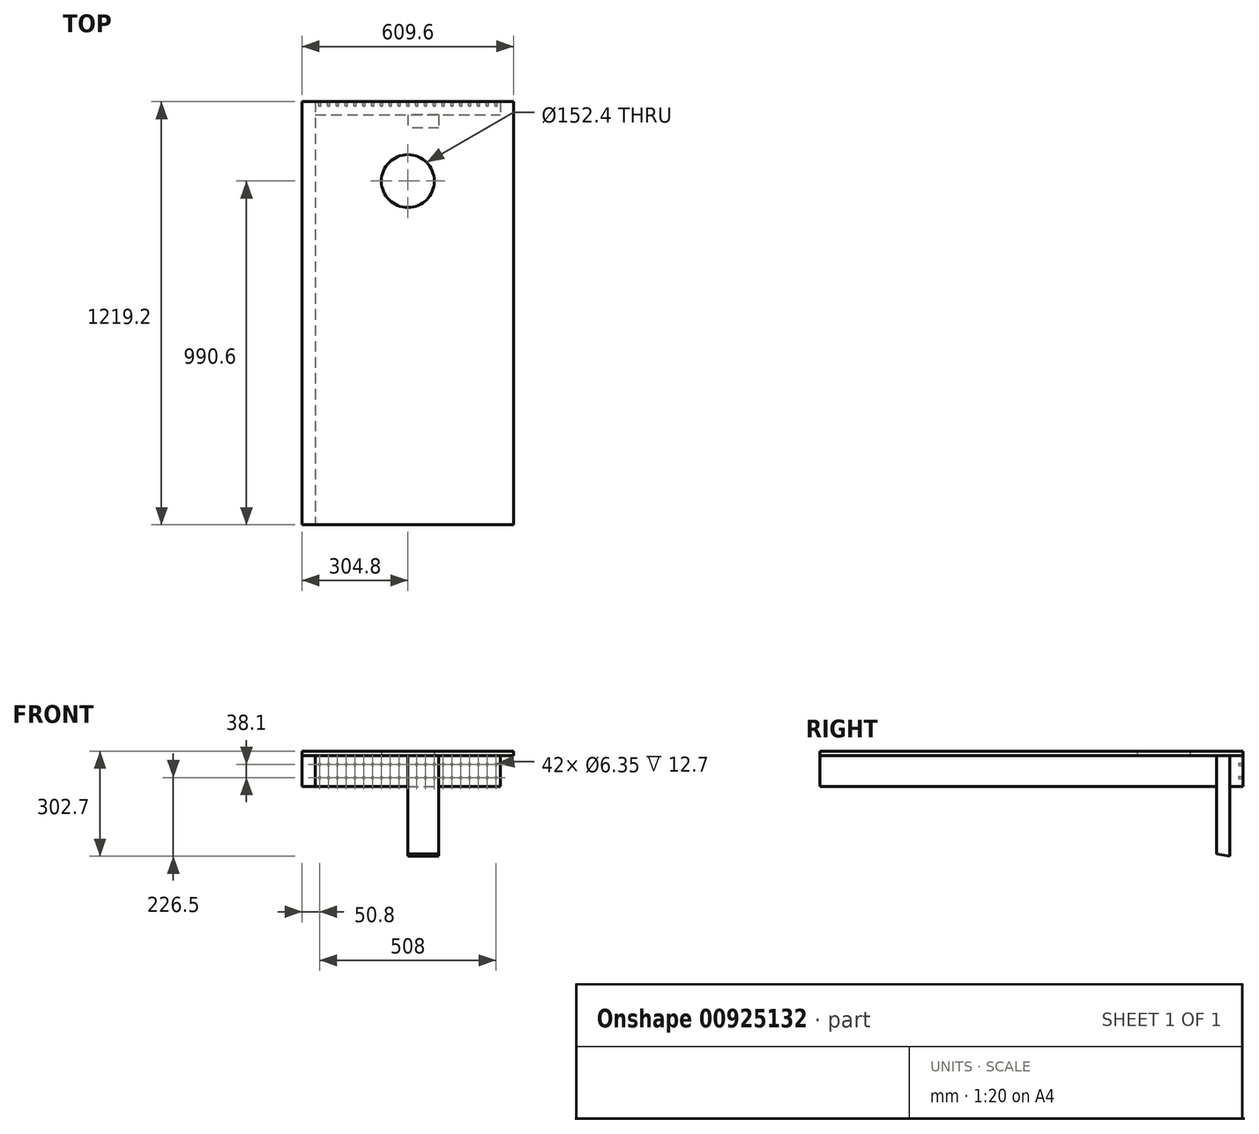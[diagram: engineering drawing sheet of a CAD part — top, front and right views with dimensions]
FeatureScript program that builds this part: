
annotation { "Feature Type Name" : "Feature", "Feature Type Description" : "" }
export const myFeature = defineFeature(function(context is Context, id is Id, definition is map)
    precondition{}
    {
        {
            assignVariable(context, id + "F0", {"name" : "sheetThickness", "anyValue" : 12.7 * mm});
        }
        {
            assignVariable(context, id + "F1", {"name" : "stockWidth", "anyValue" : 88.9 * mm});
        }
        {
            var Q0;
            Q0=qCreatedBy(makeId("Top.planeOp"),FACE);
            var sketch = newSketch(context, id + "F2", { "sketchPlane" : qUnion([Q0])});
            skLineSegment(sketch, "E0.bottom", {"start": v(304.8, -609.6) * mm, "end": v(-304.8, -609.6) * mm});
            skLineSegment(sketch, "E0.top", {"start": v(304.8, 609.6) * mm, "end": v(-304.8, 609.6) * mm});
            skLineSegment(sketch, "E0.left", {"start": v(304.8, -609.6) * mm, "end": v(304.8, 609.6) * mm});
            skLineSegment(sketch, "E0.right", {"start": v(-304.8, -609.6) * mm, "end": v(-304.8, 609.6) * mm});
            skPoint(sketch, "E0.middle", {"position": v(0, 0) * mm});
            skLineSegment(sketch, "E1", {"start": v(0, 609.6) * mm, "end": v(0, 381) * mm, "construction": true});
            skCircle(sketch, "E2", {"center": v(0, 381) * mm, "radius": 76.2 * mm});
            skLineSegment(sketch, "E3", {"start": v(-266.7, 571.5) * mm, "end": v(266.7, 571.5) * mm});
            skLineSegment(sketch, "E4", {"start": v(-266.7, -571.5) * mm, "end": v(266.7, -571.5) * mm});
            skLineSegment(sketch, "E5", {"start": v(266.7, 609.6) * mm, "end": v(266.7, -609.6) * mm});
            skLineSegment(sketch, "E6", {"start": v(-266.7, 609.6) * mm, "end": v(-266.7, -609.6) * mm});
            skLineSegment(sketch, "E7.bottom", {"start": v(-241.3, 571.5) * mm, "end": v(-152.4, 571.5) * mm});
            skLineSegment(sketch, "E7.top", {"start": v(-241.3, 533.4) * mm, "end": v(-152.4, 533.4) * mm});
            skLineSegment(sketch, "E7.left", {"start": v(-241.3, 571.5) * mm, "end": v(-241.3, 533.4) * mm});
            skLineSegment(sketch, "E7.right", {"start": v(-152.4, 571.5) * mm, "end": v(-152.4, 533.4) * mm});
            skLineSegment(sketch, "E8.bottom", {"start": v(152.4, 571.5) * mm, "end": v(241.3, 571.5) * mm});
            skLineSegment(sketch, "E8.top", {"start": v(152.4, 533.4) * mm, "end": v(241.3, 533.4) * mm});
            skLineSegment(sketch, "E8.left", {"start": v(152.4, 571.5) * mm, "end": v(152.4, 533.4) * mm});
            skLineSegment(sketch, "E8.right", {"start": v(241.3, 571.5) * mm, "end": v(241.3, 533.4) * mm});
            skLineSegment(sketch, "E9.bottom", {"start": v(266.7, -19.05) * mm, "end": v(-266.7, -19.05) * mm});
            skLineSegment(sketch, "E9.top", {"start": v(266.7, 19.05) * mm, "end": v(-266.7, 19.05) * mm});
            skLineSegment(sketch, "E9.left", {"start": v(266.7, -19.05) * mm, "end": v(266.7, 19.05) * mm});
            skLineSegment(sketch, "E9.right", {"start": v(-266.7, -19.05) * mm, "end": v(-266.7, 19.05) * mm});
            skSolve(sketch);
        }
        {
            var Q0;
            Q0=makeQuery(id+"F2.imprint","IMPRINT",FACE,{"disambiguationData":[TD([[makeQuery(id+"F2.imprint","IMPRINT",EDGE,{"derivedFrom":sQuery(id+"F2.wireOp",EDGE,"E2")}),-1.0]])]});
            var Q1;
            Q1=makeQuery(id+"F2.imprint","IMPRINT",FACE,{"disambiguationData":[TD([[makeQuery(id+"F2.imprint","IMPRINT",EDGE,{"derivedFrom":sQuery(id+"F2.wireOp",EDGE,"E7.top")}),1.0]])]});
            var Q2;
            Q2=makeQuery(id+"F2.imprint","IMPRINT",FACE,{"disambiguationData":[TD([[makeQuery(id+"F2.imprint","IMPRINT",EDGE,{"derivedFrom":sQuery(id+"F2.wireOp",EDGE,"E8.top")}),1.0]])]});
            var Q3;
            {var subQ5=sQuery(id+"F2.wireOp",EDGE,"E0.left");Q3=makeQuery(id+"F2.imprint","IMPRINT",FACE,{"disambiguationData":[TD([[makeQuery(id+"F2.imprint","IMPRINT",EDGE,{"derivedFrom":subQ5}),1.0]])]});}
            var Q4;
            {var subQ4=sQuery(id+"F2.wireOp",EDGE,"E0.top");var subQ10=sQuery(id+"F2.wireOp",EDGE,"E5");var subQ11=makeQuery(id+"F2.imprint","INTERSECT",VERTEX,{"derivedFrom":[subQ4,subQ10]});var subQ18=sQuery(id+"F2.wireOp",EDGE,"E0.left");var subQ23=sQuery(id+"F2.wireOp",EDGE,"E0.right");Q4=qUnion([makeQuery(id+"F2.imprint","IMPRINT",FACE,{"disambiguationData":[TD([[makeQuery(id+"F2.imprint","IMPRINT",EDGE,{"derivedFrom":subQ23}),-1.0]])]}),makeQuery(id+"F2.imprint","IMPRINT",FACE,{"disambiguationData":[TD([[makeQuery(id+"F2.imprint","IMPRINT",EDGE,{"derivedFrom":subQ18}),1.0]])]}),makeQuery(id+"F2.imprint","IMPRINT",FACE,{"disambiguationData":[TD([[makeQuery(id+"F2.imprint","IMPRINT",EDGE,{"disambiguationData":[TD([[subQ11,-1.0]])],"derivedFrom":subQ4}),1.0]])]})]);}
            var Q5;
            {var subQ0=sQuery(id+"F2.wireOp",EDGE,"E0.right");Q5=makeQuery(id+"F2.imprint","IMPRINT",FACE,{"disambiguationData":[TD([[makeQuery(id+"F2.imprint","IMPRINT",EDGE,{"derivedFrom":subQ0}),-1.0]])]});}
            var Q6;
            {var subQ5=sQuery(id+"F2.wireOp",EDGE,"E4");Q6=makeQuery(id+"F2.imprint","IMPRINT",FACE,{"disambiguationData":[TD([[makeQuery(id+"F2.imprint","IMPRINT",EDGE,{"derivedFrom":subQ5}),-1.0]])]});}
            var Q7;
            {var subQ0=sQuery(id+"F2.wireOp",EDGE,"E4");Q7=makeQuery(id+"F2.imprint","IMPRINT",FACE,{"disambiguationData":[TD([[makeQuery(id+"F2.imprint","IMPRINT",EDGE,{"derivedFrom":subQ0}),1.0]])]});}
            var Q8;
            {var subQ0=sQuery(id+"F2.wireOp",EDGE,"E9.bottom");Q8=makeQuery(id+"F2.imprint","IMPRINT",FACE,{"disambiguationData":[TD([[makeQuery(id+"F2.imprint","IMPRINT",EDGE,{"derivedFrom":subQ0}),-1.0]])]});}
            extrude(context, id + "F3", {"entities" : qUnion([Q0, Q1, Q2, Q3, Q4, Q5, Q6, Q7, Q8]), "depth" : getVariable(context, 'sheetThickness'), "offsetDistance" : 25.4 * mm});
        }
        {
            var Q0;
            {var subQ4=sQuery(id+"F2.wireOp",EDGE,"E0.top");var subQ9=sQuery(id+"F2.wireOp",EDGE,"E5");var subQ10=makeQuery(id+"F2.imprint","INTERSECT",VERTEX,{"derivedFrom":[subQ4,subQ9]});Q0=makeQuery(id+"F2.imprint","IMPRINT",FACE,{"disambiguationData":[TD([[makeQuery(id+"F2.imprint","IMPRINT",EDGE,{"disambiguationData":[TD([[subQ10,-1.0]])],"derivedFrom":subQ4}),1.0]])]});}
            extrude(context, id + "F4", {"entities" : qUnion([Q0]), "oppositeDirection" : true, "depth" : getVariable(context, 'stockWidth'), "offsetDistance" : 25.4 * mm});
        }
        {
            var Q0;
            {var subQ0=sQuery(id+"F2.wireOp",EDGE,"E0.right");Q0=makeQuery(id+"F2.imprint","IMPRINT",FACE,{"disambiguationData":[TD([[makeQuery(id+"F2.imprint","IMPRINT",EDGE,{"derivedFrom":subQ0}),-1.0]])]});}
            extrude(context, id + "F5", {"entities" : qUnion([Q0]), "oppositeDirection" : true, "depth" : getVariable(context, 'stockWidth'), "offsetDistance" : 25.4 * mm});
        }
        {
            var Q0;
            Q0=qCreatedBy(makeId("Right.planeOp"),FACE);
            var sketch = newSketch(context, id + "F6", { "sketchPlane" : qUnion([Q0])});
            skLineSegment(sketch, "E10.0.0", {"start": v(-609.6, 0) * mm, "end": v(609.6, 0) * mm, "construction": true});
            skLineSegment(sketch, "E10.0.1", {"start": v(609.6, 0) * mm, "end": v(609.6, -88.9) * mm, "construction": true});
            skLineSegment(sketch, "E10.0.2", {"start": v(609.6, -88.9) * mm, "end": v(-609.6, -88.9) * mm, "construction": true});
            skLineSegment(sketch, "E10.0.3", {"start": v(-609.6, -88.9) * mm, "end": v(-609.6, 0) * mm, "construction": true});
            skLineSegment(sketch, "E11.0.0", {"start": v(609.6, 0) * mm, "end": v(-609.6, 0) * mm, "construction": true});
            skLineSegment(sketch, "E11.0.1", {"start": v(-609.6, 0) * mm, "end": v(-609.6, 12.7) * mm, "construction": true});
            skLineSegment(sketch, "E11.0.2", {"start": v(-609.6, 12.7) * mm, "end": v(609.6, 12.7) * mm, "construction": true});
            skLineSegment(sketch, "E11.0.3", {"start": v(609.6, 12.7) * mm, "end": v(609.6, 0) * mm, "construction": true});
            skLineSegment(sketch, "E12", {"start": v(609.6, 12.7) * mm, "end": v(558.44, -287.78) * mm, "construction": true});
            skLineSegment(sketch, "E13", {"start": v(558.44, -287.78) * mm, "end": v(-609.6, -88.9) * mm, "construction": true});
            skLineSegment(sketch, "E14.0", {"start": v(571.5, 0) * mm, "end": v(533.4, 0) * mm});
            skLineSegment(sketch, "E15", {"start": v(571.5, 0) * mm, "end": v(571.5, -290) * mm});
            skLineSegment(sketch, "E16", {"start": v(533.4, 0) * mm, "end": v(533.4, -283.51) * mm});
            skLineSegment(sketch, "E17", {"start": v(533.4, -283.51) * mm, "end": v(571.5, -290) * mm});
            skLineSegment(sketch, "E18", {"start": v(558.44, -287.78) * mm, "end": v(838.15, -335.4) * mm, "construction": true});
            skSolve(sketch);
        }
        {
            var Q0;
            Q0=makeQuery(id+"F6.imprint","IMPRINT",FACE,{"disambiguationData":[TD([[makeQuery(id+"F6.imprint","IMPRINT",EDGE,{"derivedFrom":sQuery(id+"F6.wireOp",EDGE,"E14.0")}),1.0]])]});
            extrude(context, id + "F7", {"entities" : qUnion([Q0]), "depth" : getVariable(context, 'stockWidth'), "offsetDistance" : 25.4 * mm});
        }
        {
            var Q0;
            Q0=makeQuery(id+"F4.opExtrude","SWEPT_FACE",FACE,{"disambiguationData":[OSD([sQuery(id+"F2.wireOp",EDGE,"E0.top")])]});
            var sketch = newSketch(context, id + "F8", { "sketchPlane" : qUnion([Q0])});
            skCircle(sketch, "E19", {"center": v(-254, -63.5) * mm, "radius": 3.18 * mm});
            skCircle(sketch, "E20.0.1.0", {"center": v(-254, -25.4) * mm, "radius": 3.18 * mm});
            skCircle(sketch, "E20.1.0.0", {"center": v(-228.6, -63.5) * mm, "radius": 3.18 * mm});
            skCircle(sketch, "E20.1.1.0", {"center": v(-228.6, -25.4) * mm, "radius": 3.18 * mm});
            skCircle(sketch, "E20.2.0.0", {"center": v(-203.2, -63.5) * mm, "radius": 3.18 * mm});
            skCircle(sketch, "E20.2.1.0", {"center": v(-203.2, -25.4) * mm, "radius": 3.18 * mm});
            skCircle(sketch, "E20.3.0.0", {"center": v(-177.8, -63.5) * mm, "radius": 3.18 * mm});
            skCircle(sketch, "E20.3.1.0", {"center": v(-177.8, -25.4) * mm, "radius": 3.18 * mm});
            skCircle(sketch, "E20.4.0.0", {"center": v(-152.4, -63.5) * mm, "radius": 3.18 * mm});
            skCircle(sketch, "E20.4.1.0", {"center": v(-152.4, -25.4) * mm, "radius": 3.18 * mm});
            skCircle(sketch, "E20.5.0.0", {"center": v(-127, -63.5) * mm, "radius": 3.18 * mm});
            skCircle(sketch, "E20.5.1.0", {"center": v(-127, -25.4) * mm, "radius": 3.18 * mm});
            skCircle(sketch, "E20.6.0.0", {"center": v(-101.6, -63.5) * mm, "radius": 3.18 * mm});
            skCircle(sketch, "E20.6.1.0", {"center": v(-101.6, -25.4) * mm, "radius": 3.18 * mm});
            skCircle(sketch, "E20.7.0.0", {"center": v(-76.2, -63.5) * mm, "radius": 3.18 * mm});
            skCircle(sketch, "E20.7.1.0", {"center": v(-76.2, -25.4) * mm, "radius": 3.18 * mm});
            skCircle(sketch, "E20.8.0.0", {"center": v(-50.8, -63.5) * mm, "radius": 3.18 * mm});
            skCircle(sketch, "E20.8.1.0", {"center": v(-50.8, -25.4) * mm, "radius": 3.18 * mm});
            skCircle(sketch, "E20.9.0.0", {"center": v(-25.4, -63.5) * mm, "radius": 3.18 * mm});
            skCircle(sketch, "E20.9.1.0", {"center": v(-25.4, -25.4) * mm, "radius": 3.18 * mm});
            skCircle(sketch, "E20.10.0.0", {"center": v(0, -63.5) * mm, "radius": 3.18 * mm});
            skCircle(sketch, "E20.10.1.0", {"center": v(0, -25.4) * mm, "radius": 3.18 * mm});
            skCircle(sketch, "E20.11.0.0", {"center": v(25.4, -63.5) * mm, "radius": 3.18 * mm});
            skCircle(sketch, "E20.11.1.0", {"center": v(25.4, -25.4) * mm, "radius": 3.18 * mm});
            skCircle(sketch, "E20.12.0.0", {"center": v(50.8, -63.5) * mm, "radius": 3.18 * mm});
            skCircle(sketch, "E20.12.1.0", {"center": v(50.8, -25.4) * mm, "radius": 3.18 * mm});
            skCircle(sketch, "E20.13.0.0", {"center": v(76.2, -63.5) * mm, "radius": 3.18 * mm});
            skCircle(sketch, "E20.13.1.0", {"center": v(76.2, -25.4) * mm, "radius": 3.18 * mm});
            skCircle(sketch, "E20.14.0.0", {"center": v(101.6, -63.5) * mm, "radius": 3.18 * mm});
            skCircle(sketch, "E20.14.1.0", {"center": v(101.6, -25.4) * mm, "radius": 3.18 * mm});
            skCircle(sketch, "E20.15.0.0", {"center": v(127, -63.5) * mm, "radius": 3.18 * mm});
            skCircle(sketch, "E20.15.1.0", {"center": v(127, -25.4) * mm, "radius": 3.18 * mm});
            skCircle(sketch, "E20.16.0.0", {"center": v(152.4, -63.5) * mm, "radius": 3.18 * mm});
            skCircle(sketch, "E20.16.1.0", {"center": v(152.4, -25.4) * mm, "radius": 3.18 * mm});
            skCircle(sketch, "E20.17.0.0", {"center": v(177.8, -63.5) * mm, "radius": 3.18 * mm});
            skCircle(sketch, "E20.17.1.0", {"center": v(177.8, -25.4) * mm, "radius": 3.18 * mm});
            skCircle(sketch, "E20.18.0.0", {"center": v(203.2, -63.5) * mm, "radius": 3.18 * mm});
            skCircle(sketch, "E20.18.1.0", {"center": v(203.2, -25.4) * mm, "radius": 3.18 * mm});
            skCircle(sketch, "E20.19.0.0", {"center": v(228.6, -63.5) * mm, "radius": 3.18 * mm});
            skCircle(sketch, "E20.19.1.0", {"center": v(228.6, -25.4) * mm, "radius": 3.18 * mm});
            skCircle(sketch, "E20.20.0.0", {"center": v(254, -63.5) * mm, "radius": 3.18 * mm});
            skCircle(sketch, "E20.20.1.0", {"center": v(254, -25.4) * mm, "radius": 3.18 * mm});
            skLineSegment(sketch, "E20.direction1", {"start": v(-254, -63.5) * mm, "end": v(-228.6, -63.5) * mm, "construction": true});
            skLineSegment(sketch, "E20.direction2", {"start": v(-254, -63.5) * mm, "end": v(-254, -25.4) * mm, "construction": true});
            skSolve(sketch);
        }
        {
            var Q0;
            Q0 = qSketchRegion(id + "F8", true);
            extrude(context, id + "F9", {"entities" : qUnion([Q0]), "operationType" : NewBodyOperationType.REMOVE, "oppositeDirection" : true, "depth" : 12.7 * mm, "offsetDistance" : 25.4 * mm});
        }
    });
